# Revit family: QF_VOLLRATH_FC-4CP-03120-RFF
name_source: partatom
category: Specialty Equipment
revit_build: Autodesk Revit 2016 (Build: 20150220_1215(x64)
units: mm (PartAtom-declared; Revit-internal decimal feet)

## family parameters
Always vertical = Yes
Cut with Voids When Loaded = Yes
OmniClass Number = 23.40.40.14.24.14
OmniClass Title = Service Line Equipment
Part Type = Normal
Room Calculation Point = No
Round Connector Dimension = Use Diameter
Shared = No
Work Plane-Based = Yes

## types (1)
- FC-4CP-03120-RFF
    Apparent Power = 384 VA
    Assembly Code = E1090320
    Conn Plug = NEMA 5-15P
    Cycle = 60 Hz
    Default Elevation = 0"
    Description = THREE-WELL 120-VOLT STANDARD REFRIGERATED MODULAR DROP-IN COLD WELL WITH FLAT FLANGE
    Direct Waste Connection Height = 0"
    Direct Waste Flow = 0 GPM
    Direct Waste RI Height = 0"
    Direct Waste Size = 1"
    FL Amps = 3 A
    HP = 0.5
    Manufacturer = VOLLRATH US
    Max Overcurrent Protection = 10 A
    Min Ckt Ampacity = 0 A
    Model = FC-4CP-03120-RFF
    Number of Poles = 1
    Phase = 1
    URL = www.vollrathfoodservice.com
    URL Cutsheet = www.vollrathfoodservice.com
    Volts = 120 V
    Watts = 384 W
    Weight in Pounds = 120

## geometry (parser evidence)
native form markers: Sweep x2
no freeform markers — native parametric forms only
